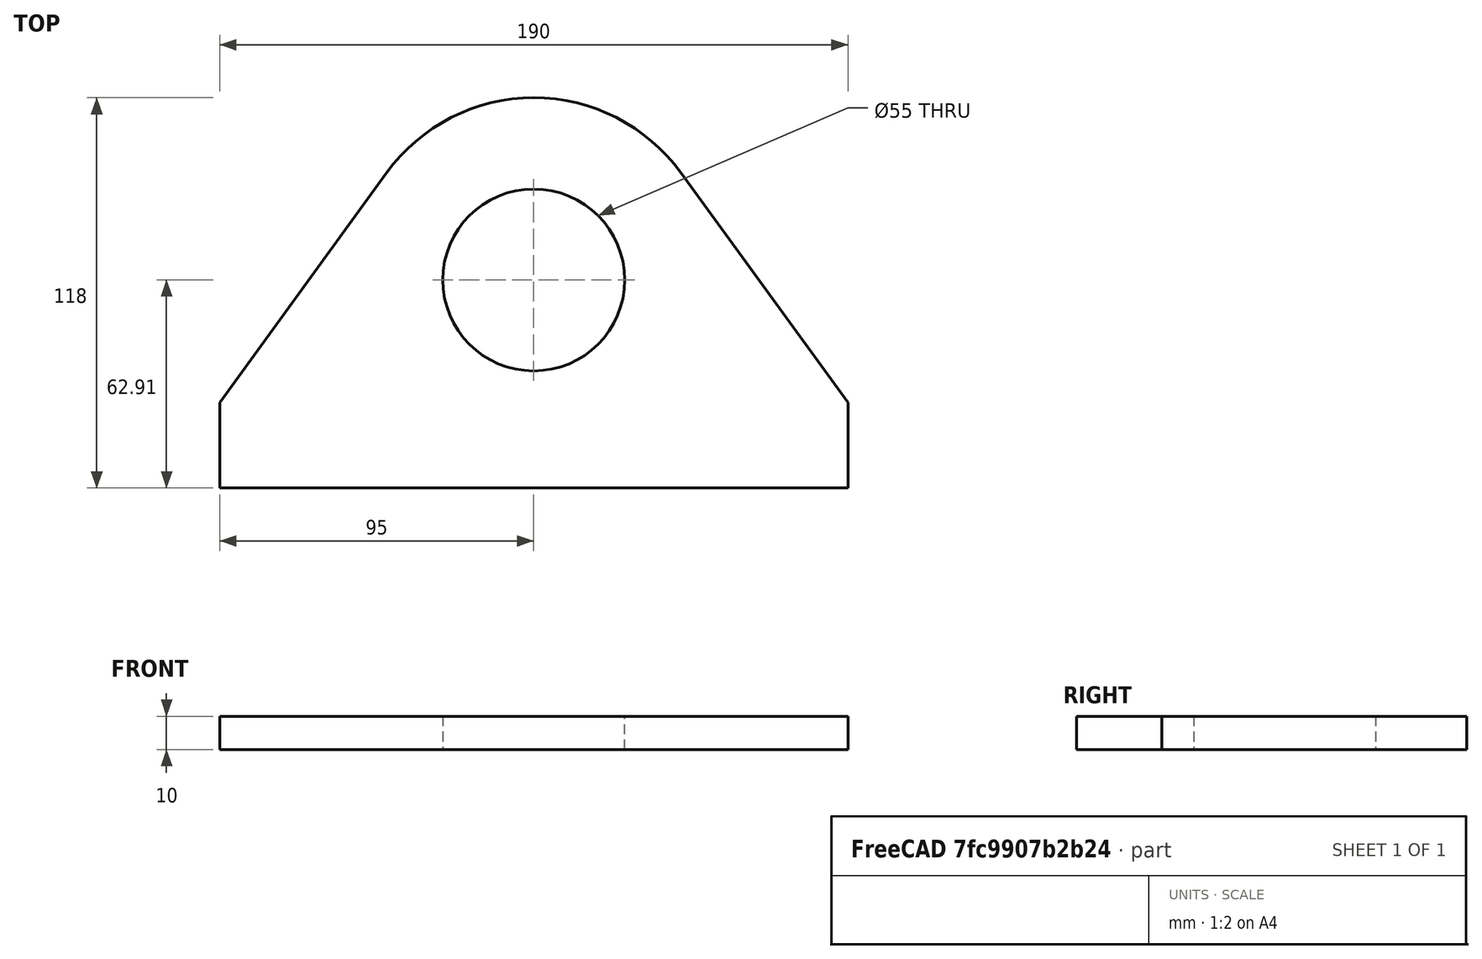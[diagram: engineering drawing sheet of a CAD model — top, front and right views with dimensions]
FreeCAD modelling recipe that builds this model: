
FCSTD DOCUMENT  (FreeCAD 1.0R39319 (Git))
Label: comp26_16mm_plate
License: All rights reserved
LicenseURL: https://en.wikipedia.org/wiki/All_rights_reserved
objects: Sketcher::SketchObject×1, PartDesign::Pad×1, PartDesign::Body×1
note: 6 computed .brp shape members not serialized (recipe doc carries the construction recipe); baked Part::Feature solids carry a one-line shape summary decoded from their .brp

FEATURE [Sketcher::SketchObject] Sketch
  ArcFitTolerance = 1e-06
  AttachmentSupport = -> [XY_Plane]
  FullyConstrained = true
  MakeInternals = false
  MapMode = 5
  sketch-geometry (8):
    g0: Circle CenterX=0 CenterY=62.91 CenterZ=0 NormalX=0 NormalY=0 NormalZ=1 AngleXU=0 Radius=27.5
    g1: LineSegment StartX=-95 StartY=0 StartZ=0 EndX=-95 EndY=25.8153 EndZ=0
    g2: LineSegment StartX=-95 StartY=25.8153 StartZ=0 EndX=-44.4959 EndY=95.3282 EndZ=0
    g3: ArcOfCircle CenterX=0 CenterY=63 CenterZ=0 NormalX=0 NormalY=0 NormalZ=1 AngleXU=0 Radius=55 StartAngle=1.5708 EndAngle=2.51327
    g4: ArcOfCircle CenterX=0 CenterY=63 CenterZ=0 NormalX=0 NormalY=0 NormalZ=1 AngleXU=0 Radius=55 StartAngle=0.628319 EndAngle=1.5708
    g5: LineSegment StartX=95 StartY=25.8153 StartZ=0 EndX=44.4959 EndY=95.3282 EndZ=0
    g6: LineSegment StartX=95 StartY=0 StartZ=0 EndX=95 EndY=25.8153 EndZ=0
    g7: LineSegment StartX=-95 StartY=0 StartZ=0 EndX=95 EndY=0 EndZ=0
  constraints (23):
    c: PointOnObject(g0,g-2)
    c: PointOnObject(g1,g-1)
    c: Vertical(g1)
    c: Coincident(g1,g2)
    c: Tangent(g2,g3) = 1.5708
    c: PointOnObject(g3,g-2)
    c: Diameter(g0) = 55
    c: Radius(g3) = 55
    c: DistanceY(g-1,g0) = 62.91
    c: DistanceY(g-1,g3) = 118
    c: Distance(g-2,g1) = 95
    c: Angle(g-1,g2) = 0.942478
    c: PointOnObject(g3,g-2)
    c: Vertical(g6)
    c: Coincident(g6,g5)
    c: Tangent(g5,g4) = -1.5708
    c: Radius(g4) = 55
    c: Coincident(g7,g1)
    c: Coincident(g7,g6)
    c: Horizontal(g7)
    c: Block(g5)
    c: Block(g6)
    c: Block(g4)
FEATURE [PartDesign::Pad] Pad
  Direction = (0,0,1)
  Length = 10
  Length2 = 10
  Profile = -> Sketch
  ReferenceAxis = -> Sketch [N_Axis]
  Refine = true
  Suppressed = false
  Type = 0
FEATURE [PartDesign::Body] Body
  AllowCompound = false
  Group = -> [Sketch,Pad]
  Origin = -> Origin
  Tip = -> Pad
